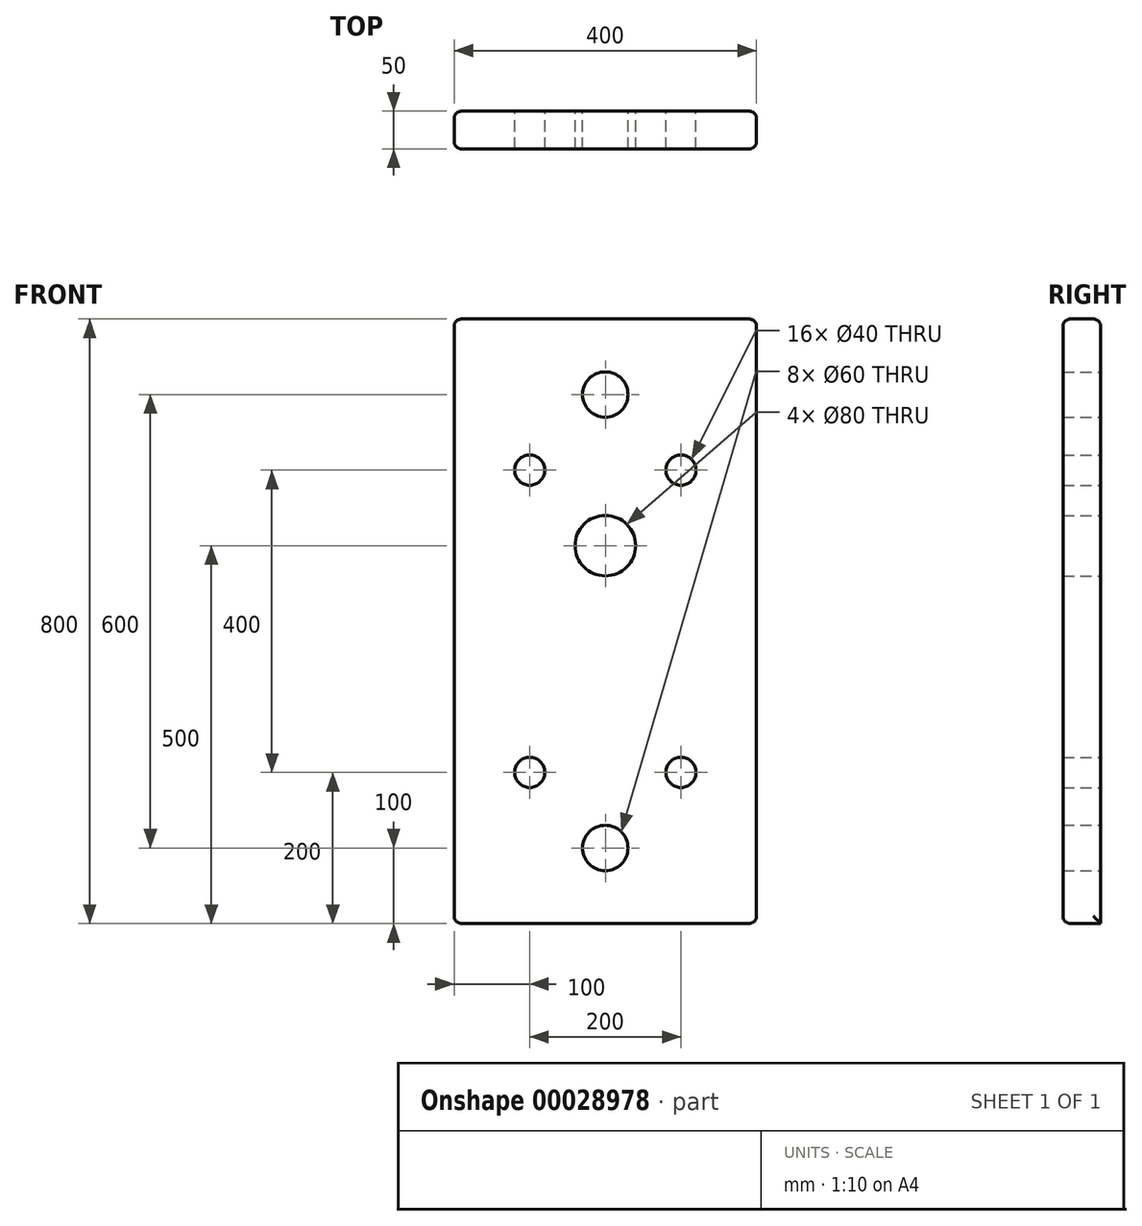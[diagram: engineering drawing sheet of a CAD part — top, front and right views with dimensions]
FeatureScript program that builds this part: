
annotation { "Feature Type Name" : "Feature", "Feature Type Description" : "" }
export const myFeature = defineFeature(function(context is Context, id is Id, definition is map)
    precondition{}
    {
        {
            var Q0;
            Q0=qCreatedBy(makeId("Front.planeOp"),FACE);
            var sketch = newSketch(context, id + "F0", { "sketchPlane" : qUnion([Q0])});
            skCircle(sketch, "E0", {"center": v(0, 0) * mm, "radius": 30 * mm});
            skCircle(sketch, "E1", {"center": v(-100, -100) * mm, "radius": 20 * mm});
            skCircle(sketch, "E2.0.1.0", {"center": v(-100, -500) * mm, "radius": 20 * mm});
            skCircle(sketch, "E2.1.0.0", {"center": v(100, -100) * mm, "radius": 20 * mm});
            skCircle(sketch, "E2.1.1.0", {"center": v(100, -500) * mm, "radius": 20 * mm});
            skLineSegment(sketch, "E2.direction1", {"start": v(-100, -100) * mm, "end": v(100, -100) * mm, "construction": true});
            skLineSegment(sketch, "E2.direction2", {"start": v(-100, -100) * mm, "end": v(-100, -500) * mm, "construction": true});
            skCircle(sketch, "E3", {"center": v(0, -600) * mm, "radius": 30 * mm});
            skLineSegment(sketch, "E4.bottom", {"start": v(-200, 100) * mm, "end": v(200, 100) * mm});
            skLineSegment(sketch, "E4.top", {"start": v(-200, -700) * mm, "end": v(200, -700) * mm});
            skLineSegment(sketch, "E4.left", {"start": v(-200, 100) * mm, "end": v(-200, -700) * mm});
            skLineSegment(sketch, "E4.right", {"start": v(200, 100) * mm, "end": v(200, -700) * mm});
            skCircle(sketch, "E5", {"center": v(0, -200) * mm, "radius": 40 * mm});
            skSolve(sketch);
        }
        {
            var Q0;
            Q0 = qSketchRegion(id + "F0", true);
            extrude(context, id + "F1", {"entities" : qUnion([Q0]), "depth" : 50 * mm});
        }
        {
            var Q0;
            Q0=makeQuery(id+"F1.opExtrude","SWEPT_FACE",FACE,{"disambiguationData":[OSD([sQuery(id+"F0.wireOp",EDGE,"E4.left")])]});
            var Q1;
            Q1=makeQuery(id+"F1.opExtrude","CAP_EDGE",EDGE,{"disambiguationData":[OSD([sQuery(id+"F0.wireOp",EDGE,"E4.top")])],"isStart":false});
            var Q2;
            Q2=makeQuery(id+"F1.opExtrude","SWEPT_FACE",FACE,{"disambiguationData":[OSD([sQuery(id+"F0.wireOp",EDGE,"E4.right")])]});
            var Q3;
            Q3=makeQuery(id+"F1.opExtrude","SWEPT_FACE",FACE,{"disambiguationData":[OSD([sQuery(id+"F0.wireOp",EDGE,"E4.bottom")])]});
            fillet(context, id + "F2", {"entities" : qUnion([Q0, Q1, Q2, Q3]), "radius" : 10 * mm, "tangentPropagation" : true, "allowEdgeOverflow" : false});
        }
    });
